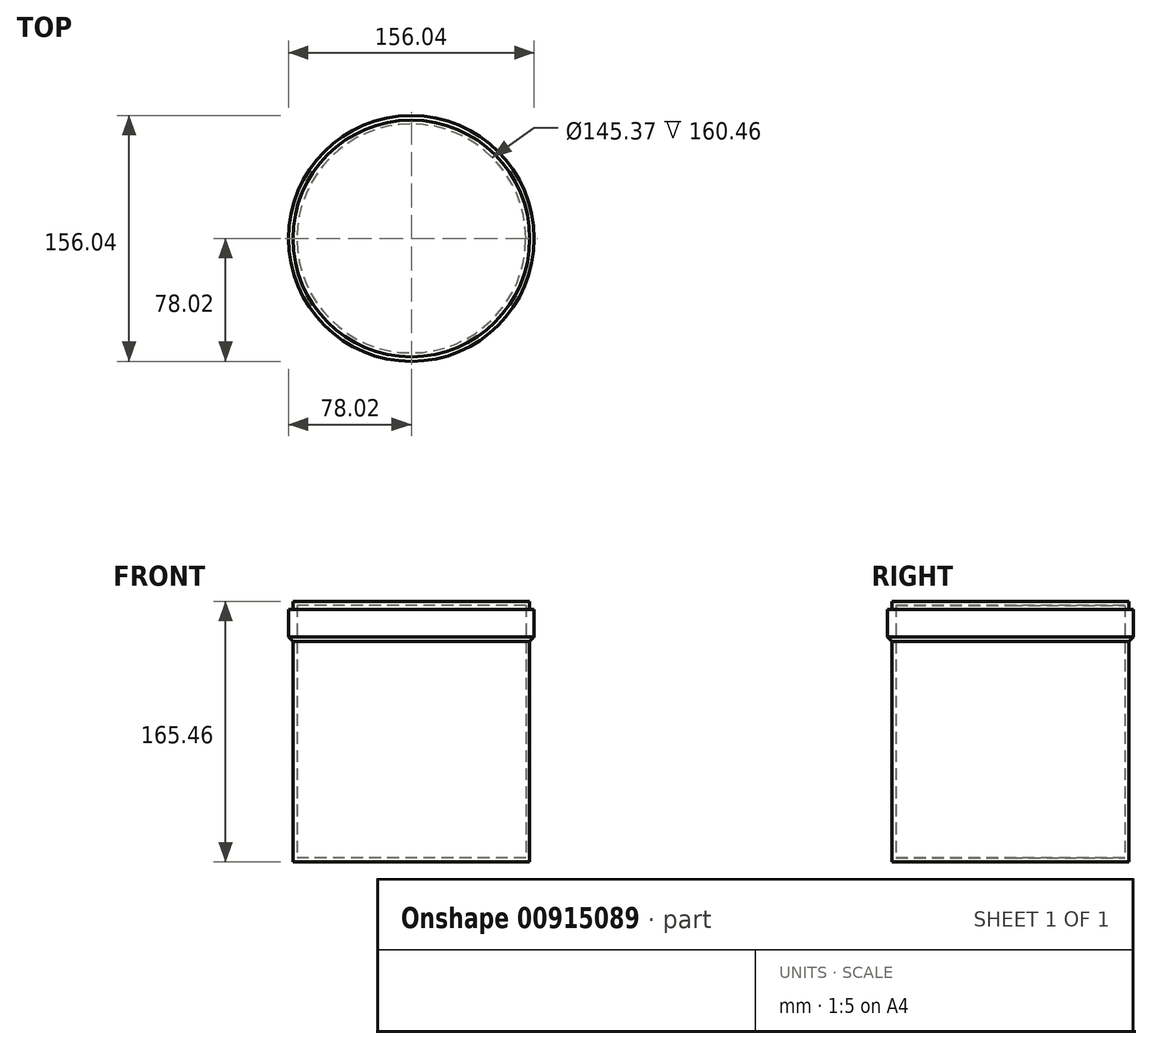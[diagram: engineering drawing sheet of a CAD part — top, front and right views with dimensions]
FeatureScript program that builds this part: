
annotation { "Feature Type Name" : "Feature", "Feature Type Description" : "" }
export const myFeature = defineFeature(function(context is Context, id is Id, definition is map)
    precondition{}
    {
        {
            var Q0;
            Q0=qCreatedBy(makeId("Top.planeOp"),FACE);
            var sketch = newSketch(context, id + "F0", { "sketchPlane" : qUnion([Q0])});
            skCircle(sketch, "E0", {"center": v(0, 0) * mm, "radius": 72.68 * mm});
            skSolve(sketch);
        }
        {
            var Q0;
            Q0=makeQuery(id+"F0.imprint","IMPRINT",FACE,{"disambiguationData":[TD([[makeQuery(id+"F0.imprint","IMPRINT",EDGE,{"derivedFrom":sQuery(id+"F0.wireOp",EDGE,"E0")}),1.0]])]});
            extrude(context, id + "F1", {"entities" : qUnion([Q0]), "oppositeDirection" : true, "depth" : 135.46 * mm, "offsetDistance" : 25 * mm, "hasDraft" : true, "draftAngle" : 0 * degree, "draftPullDirection" : true, "hasSecondDirection" : true, "secondDirectionOppositeDirection" : false, "secondDirectionDepth" : 22.15 * mm});
        }
        {
            var Q0;
            Q0 = qSketchRegion(id + "F0", true);
            var sketch = newSketch(context, id + "F2", { "sketchPlane" : qUnion([Q0])});
            skSolve(sketch);
        }
        {
            var Q0;
            Q0=makeQuery(id+"F2.imprint","IMPRINT",FACE,{"disambiguationData":[TD([[makeQuery(id+"F2.imprint","IMPRINT",EDGE,{"derivedFrom":makeQuery(id+"F0.imprint","IMPRINT",EDGE,{"derivedFrom":sQuery(id+"F0.wireOp",EDGE,"E0")})}),1.0]])]});
            extrude(context, id + "F3", {"entities" : qUnion([Q0]), "operationType" : NewBodyOperationType.ADD, "depth" : 25 * mm, "offsetDistance" : 25 * mm});
        }
        {
            var Q0;
            Q0=makeQuery(id+"F3.opExtrude","CAP_FACE",FACE,{"disambiguationData":[OSD([sQuery(id+"F0.wireOp",EDGE,"E0")])],"isStart":false});
            var Q1;
            Q1=makeQuery(id+"F1.*.split.splitOp","SPLIT",BODY,{"derivedFrom":makeQuery(id+"F1.opExtrude","SWEPT_BODY",BODY,{"disambiguationData":[OSD([sQuery(id+"F0.wireOp",EDGE,"E0")])]})});
            shell(context, id + "F4", {"isHollow" : true, "entities" : qUnion([Q0]), "parts" : qUnion([Q1]), "thickness" : 2.5 * mm, "oppositeDirection" : true});
        }
        {
            var Q0;
            Q0 = qSketchRegion(id + "F0", true);
            var sketch = newSketch(context, id + "F5", { "sketchPlane" : qUnion([Q0])});
            skCircle(sketch, "E1", {"center": v(0, 0) * mm, "radius": 78.02 * mm});
            skSolve(sketch);
        }
        {
            var Q0;
            Q0=makeQuery(id+"F5.imprint","IMPRINT",FACE,{"disambiguationData":[TD([[makeQuery(id+"F5.imprint","IMPRINT",EDGE,{"derivedFrom":sQuery(id+"F5.wireOp",EDGE,"E1")}),1.0]])]});
            var Q1;
            Q1=sQuery(id+"F5.wireOp",EDGE,"E1");
            extrude(context, id + "F6", {"entities" : qUnion([Q0]), "operationType" : NewBodyOperationType.ADD, "surfaceEntities" : qUnion([Q1]), "depth" : 22.3 * mm, "offsetDistance" : 25 * mm, "hasDraft" : true, "draftAngle" : 0 * degree, "draftPullDirection" : true});
        }
        {
            var Q0;
            Q0=makeQuery(id+"F6.opExtrude","CAP_EDGE",EDGE,{"disambiguationData":[OSD([sQuery(id+"F5.wireOp",EDGE,"E1")])],"isStart":true});
            chamfer(context, id + "F7", {"entities" : qUnion([Q0]), "width" : 5 * mm, "tangentPropagation" : true});
        }
    });
